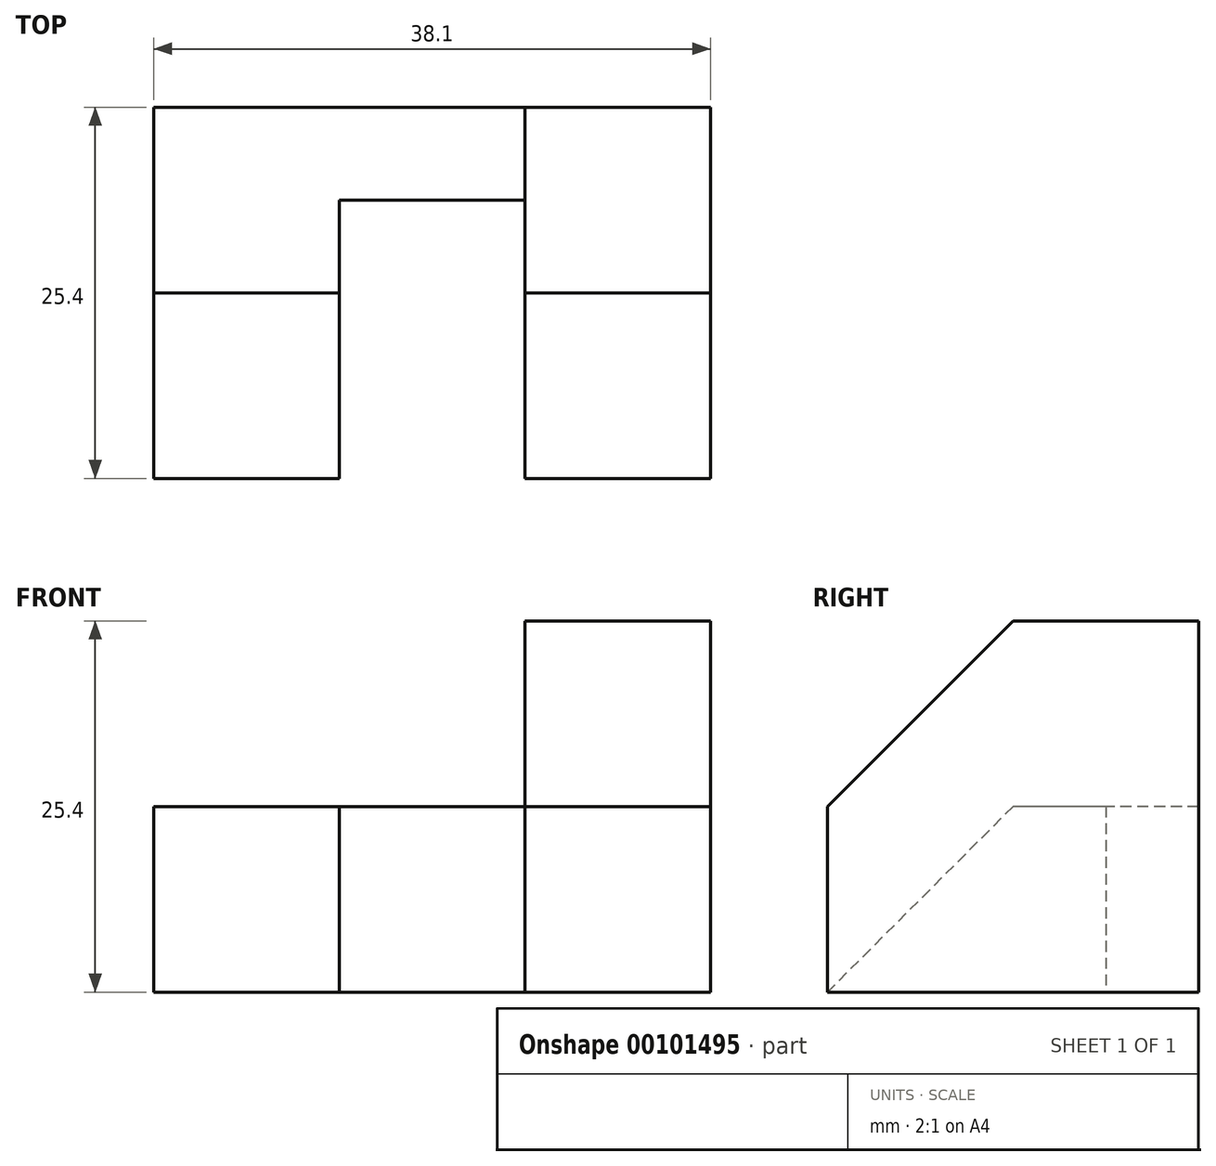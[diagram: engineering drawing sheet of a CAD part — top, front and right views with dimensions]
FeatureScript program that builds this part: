
annotation { "Feature Type Name" : "Feature", "Feature Type Description" : "" }
export const myFeature = defineFeature(function(context is Context, id is Id, definition is map)
    precondition{}
    {
        {
            var Q0;
            Q0=qCreatedBy(makeId("Right.planeOp"),FACE);
            var sketch = newSketch(context, id + "F0", { "sketchPlane" : qUnion([Q0])});
            skLineSegment(sketch, "E0", {"start": v(0, 0) * mm, "end": v(25.4, 0) * mm});
            skLineSegment(sketch, "E1", {"start": v(25.4, 0) * mm, "end": v(25.4, 25.4) * mm});
            skLineSegment(sketch, "E2", {"start": v(25.4, 25.4) * mm, "end": v(12.7, 25.4) * mm});
            skLineSegment(sketch, "E3", {"start": v(12.7, 25.4) * mm, "end": v(0, 12.7) * mm});
            skLineSegment(sketch, "E4", {"start": v(0, 12.7) * mm, "end": v(0, 0) * mm});
            skSolve(sketch);
        }
        {
            var Q0;
            Q0=makeQuery(id+"F0.imprint","IMPRINT",FACE,{"disambiguationData":[TD([[makeQuery(id+"F0.imprint","IMPRINT",EDGE,{"derivedFrom":sQuery(id+"F0.wireOp",EDGE,"E0")}),1.0]])]});
            extrude(context, id + "F1", {"entities" : qUnion([Q0]), "depth" : 12.7 * mm});
        }
        {
            var Q0;
            Q0=makeQuery(id+"F1.opExtrude","CAP_FACE",FACE,{"disambiguationData":[OSD([sQuery(id+"F0.wireOp",EDGE,"E0"),sQuery(id+"F0.wireOp",EDGE,"E1"),sQuery(id+"F0.wireOp",EDGE,"E2"),sQuery(id+"F0.wireOp",EDGE,"E3"),sQuery(id+"F0.wireOp",EDGE,"E4")])],"isStart":true});
            var sketch = newSketch(context, id + "F2", { "sketchPlane" : qUnion([Q0])});
            skLineSegment(sketch, "E5", {"start": v(-25.4, 12.7) * mm, "end": v(-12.7, 12.7) * mm});
            skLineSegment(sketch, "E6", {"start": v(-12.7, 12.7) * mm, "end": v(0, 0) * mm});
            skSolve(sketch);
        }
        {
            var Q0;
            {var subQ0=sQuery(id+"F2.wireOp",EDGE,"E5");Q0=makeQuery(id+"F2.imprint","IMPRINT",FACE,{"disambiguationData":[TD([[makeQuery(id+"F2.imprint","IMPRINT",EDGE,{"derivedFrom":subQ0}),-1.0]])]});}
            extrude(context, id + "F3", {"entities" : qUnion([Q0]), "operationType" : NewBodyOperationType.ADD, "depth" : 25.4 * mm});
        }
        {
            var Q0;
            {var subQ0=sQuery(id+"F0.wireOp",EDGE,"E0");Q0=makeQuery(id+"F3.boolean.opBoolean","MERGE",FACE,{"derivedFrom":[makeQuery(id+"F1.opExtrude","SWEPT_FACE",FACE,{"disambiguationData":[OSD([subQ0])]}),makeQuery(id+"F3.opExtrude","SWEPT_FACE",FACE,{"disambiguationData":[OSD([subQ0])]})]});}
            var sketch = newSketch(context, id + "F4", { "sketchPlane" : qUnion([Q0])});
            skLineSegment(sketch, "E7", {"start": v(0, 0) * mm, "end": v(0, -19.05) * mm});
            skLineSegment(sketch, "E8", {"start": v(-12.7, 0) * mm, "end": v(-12.7, -19.05) * mm});
            skLineSegment(sketch, "E9", {"start": v(-12.7, -19.05) * mm, "end": v(0, -19.05) * mm});
            skSolve(sketch);
        }
        {
            var Q0;
            {var subQ0=sQuery(id+"F4.wireOp",EDGE,"E7");Q0=makeQuery(id+"F4.imprint","IMPRINT",FACE,{"disambiguationData":[TD([[makeQuery(id+"F4.imprint","IMPRINT",EDGE,{"derivedFrom":subQ0}),-1.0]])]});}
            extrude(context, id + "F5", {"entities" : qUnion([Q0]), "operationType" : NewBodyOperationType.REMOVE, "endBound" : BoundingType.THROUGH_ALL, "oppositeDirection" : true, "depth" : 25.4 * mm});
        }
    });
